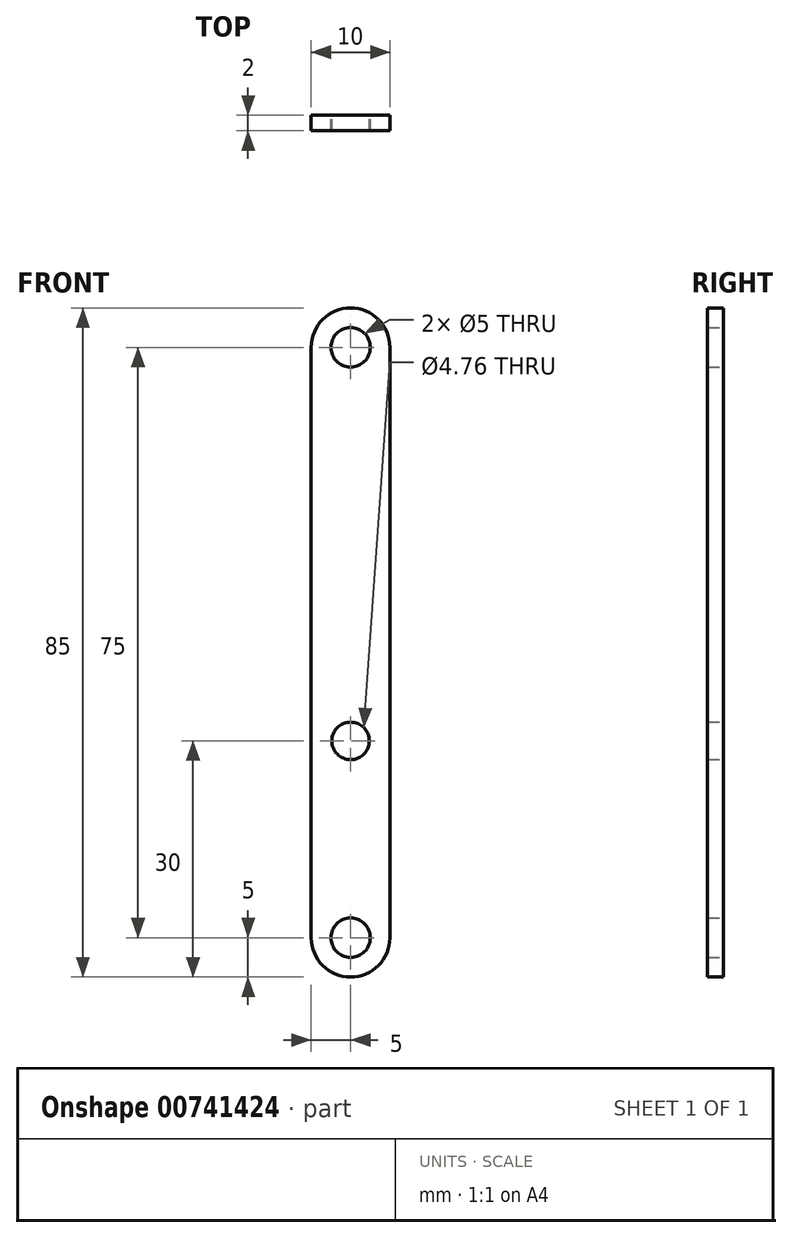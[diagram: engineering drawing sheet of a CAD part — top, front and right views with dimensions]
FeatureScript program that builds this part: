
annotation { "Feature Type Name" : "Feature", "Feature Type Description" : "" }
export const myFeature = defineFeature(function(context is Context, id is Id, definition is map)
    precondition{}
    {
        {
            var Q0;
            Q0=qCreatedBy(makeId("Front.planeOp"),FACE);
            var sketch = newSketch(context, id + "F0", { "sketchPlane" : qUnion([Q0])});
            skCircle(sketch, "E0", {"center": v(0, 46.24) * mm, "radius": 2.5 * mm});
            skCircle(sketch, "E1", {"center": v(0, -28.76) * mm, "radius": 2.5 * mm});
            skArc(sketch, "E2", {"start": v(5, 46.24) * mm, "mid": v(0, 51.24) * mm, "end": v(-5, 46.24) * mm});
            skArc(sketch, "E3", {"start": v(-5, -28.76) * mm, "mid": v(0, -33.76) * mm, "end": v(5, -28.76) * mm});
            skLineSegment(sketch, "E4", {"start": v(-5, 46.24) * mm, "end": v(-5, -28.76) * mm});
            skLineSegment(sketch, "E5", {"start": v(5, 46.24) * mm, "end": v(5, -28.76) * mm});
            skCircle(sketch, "E6", {"center": v(0, -3.76) * mm, "radius": 2.38 * mm});
            skSolve(sketch);
        }
        {
            var Q0;
            Q0=makeQuery(id+"F0.imprint","IMPRINT",FACE,{"disambiguationData":[TD([[makeQuery(id+"F0.imprint","IMPRINT",EDGE,{"derivedFrom":sQuery(id+"F0.wireOp",EDGE,"E0")}),-1.0]])]});
            extrude(context, id + "F1", {"entities" : qUnion([Q0]), "depth" : 2 * mm, "offsetDistance" : 25.4 * mm});
        }
    });
